# Revit family: Toilet-Floor_Mount-Elongated-American_Standard-Studio-2794.204.020
name_source: partatom
category: Plumbing Fixtures
revit_build: Autodesk Revit 2015 (Build: 20140606_1530(x64)
units: mm (PartAtom-declared; Revit-internal decimal feet)

## types (1)
- 2794.204.020
    Assembly Code = D2010110
    Bowl Shape = Elongated
    CW Connection = Yes
    CWFU = 5
    Cold Water Connection Diameter = 1/2"
    Cold Water Connection Height = 5 1/2"
    Cold Water Connection Radius = 1/4"
    Cold Water Connection Width = 2 1/4"
    Default Elevation = 0"
    Description = Studio Concealed Trapway Dual Flush Right Height Elongated Toilet With Seat.
    Finish = Plastic-American Standard-020-White
    Flush Rate = 1.6 gpf (6.0Lpf)/1.1 gpf(4.1Lpf)
    HW Connection = No
    HWFU = 0
    Height = 30 7/8"
    Installation Type = Floor Mounted
    Length = 30 1/4"
    Manufacturer = American Standard
    Material = Vitreous China-American Standard-020-White
    Model = 2794.204.020
    Price = Prices may vary. Please consult Manufacturer Representative for most up-to-date price list.
    Product Documentation Link = https://www.americanstandard-us.com
    Product Page URL = https://www.americanstandard-us.com
    Revised Date = 01/17/2017
    Seat Specification = American Standard #5218.110 Duroplast Slow- Close seat and cover, with easy lift-off feature for simple removal and attachment for cleaning, packed with bowl. Telescoping cover conceals seat ring when closed.
    Shipping Weight = 113lbs (51.6kg)
    URL = http://www.americanstandard.ca
    Vent Connection = No
    WFU = 5
    Warranty Information = Lifetime warranty on chinaware, 5 year warranty on all mechanical parts, and 1 year warranty on seat
    Waste Connection = Yes
    Waste Connection Diameter = 2 1/8"
    Waste Connection Radius = 1 1/16"
    Width = 15 3/4"

## geometry (parser evidence)
native form markers: Sweep x2
no freeform markers — native parametric forms only
